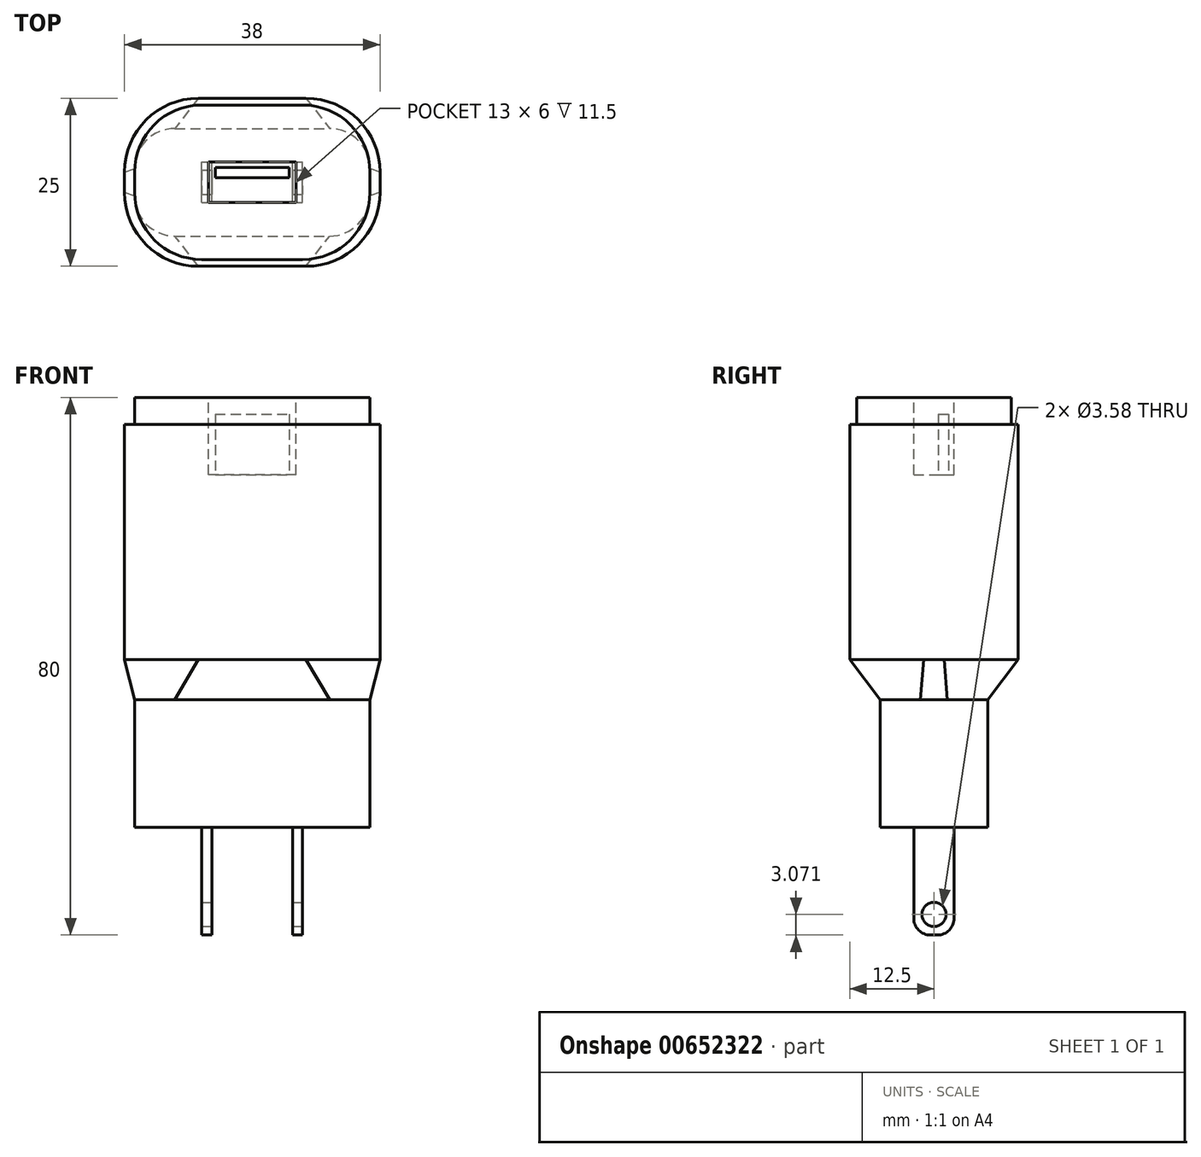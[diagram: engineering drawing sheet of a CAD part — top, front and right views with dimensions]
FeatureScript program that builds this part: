
annotation { "Feature Type Name" : "Feature", "Feature Type Description" : "" }
export const myFeature = defineFeature(function(context is Context, id is Id, definition is map)
    precondition{}
    {
        {
            var Q0;
            Q0=qCreatedBy(makeId("Top.planeOp"),FACE);
            var sketch = newSketch(context, id + "F0", { "sketchPlane" : qUnion([Q0])});
            skLineSegment(sketch, "E0.bottom", {"start": v(-19, -12.5) * mm, "end": v(19, -12.5) * mm});
            skLineSegment(sketch, "E0.top", {"start": v(-19, 12.5) * mm, "end": v(19, 12.5) * mm});
            skLineSegment(sketch, "E0.left", {"start": v(-19, -12.5) * mm, "end": v(-19, 12.5) * mm});
            skLineSegment(sketch, "E0.right", {"start": v(19, -12.5) * mm, "end": v(19, 12.5) * mm});
            skPoint(sketch, "E0.middle", {"position": v(0, 0) * mm});
            skSolve(sketch);
        }
        {
            var Q0;
            Q0=makeQuery(id+"F0.imprint","IMPRINT",FACE,{"disambiguationData":[TD([[makeQuery(id+"F0.imprint","IMPRINT",EDGE,{"derivedFrom":sQuery(id+"F0.wireOp",EDGE,"E0.bottom")}),1.0]])]});
            extrude(context, id + "F1", {"entities" : qUnion([Q0]), "depth" : 35 * mm, "offsetDistance" : 25.4 * mm});
        }
        {
            var Q0;
            Q0=makeQuery(id+"F1.opExtrude","SWEPT_EDGE",EDGE,{"disambiguationData":[OSD([sQuery(id+"F0.wireOp",EDGE,"E0.bottom"),sQuery(id+"F0.wireOp",EDGE,"E0.right")])]});
            var Q1;
            Q1=makeQuery(id+"F1.opExtrude","SWEPT_EDGE",EDGE,{"disambiguationData":[OSD([sQuery(id+"F0.wireOp",EDGE,"E0.bottom"),sQuery(id+"F0.wireOp",EDGE,"E0.left")])]});
            var Q2;
            Q2=makeQuery(id+"F1.opExtrude","SWEPT_EDGE",EDGE,{"disambiguationData":[OSD([sQuery(id+"F0.wireOp",EDGE,"E0.top"),sQuery(id+"F0.wireOp",EDGE,"E0.right")])]});
            var Q3;
            Q3=makeQuery(id+"F1.opExtrude","SWEPT_EDGE",EDGE,{"disambiguationData":[OSD([sQuery(id+"F0.wireOp",EDGE,"E0.top"),sQuery(id+"F0.wireOp",EDGE,"E0.left")])]});
            fillet(context, id + "F2", {"entities" : qUnion([Q0, Q1, Q2, Q3]), "radius" : 11 * mm, "tangentPropagation" : true, "allowEdgeOverflow" : false});
        }
        {
            var Q0;
            Q0=qCreatedBy(makeId("Top.planeOp"),FACE);
            var sketch = newSketch(context, id + "F3", { "sketchPlane" : qUnion([Q0])});
            skLineSegment(sketch, "E1.bottom", {"start": v(17.5, -11.5) * mm, "end": v(-17.5, -11.5) * mm});
            skLineSegment(sketch, "E1.top", {"start": v(17.5, 11.5) * mm, "end": v(-17.5, 11.5) * mm});
            skLineSegment(sketch, "E1.left", {"start": v(17.5, -11.5) * mm, "end": v(17.5, 11.5) * mm});
            skLineSegment(sketch, "E1.right", {"start": v(-17.5, -11.5) * mm, "end": v(-17.5, 11.5) * mm});
            skPoint(sketch, "E1.middle", {"position": v(0, 0) * mm});
            skSolve(sketch);
        }
        {
            var Q0;
            Q0 = qSketchRegion(id + "F3", true);
            extrude(context, id + "F4", {"entities" : qUnion([Q0]), "operationType" : NewBodyOperationType.ADD, "depth" : 39 * mm, "offsetDistance" : 25 * mm});
        }
        {
            var Q0;
            Q0=makeQuery(id+"F4.opExtrude","SWEPT_EDGE",EDGE,{"disambiguationData":[OSD([sQuery(id+"F3.wireOp",EDGE,"E1.bottom"),sQuery(id+"F3.wireOp",EDGE,"E1.right")])]});
            var Q1;
            Q1=makeQuery(id+"F4.opExtrude","SWEPT_EDGE",EDGE,{"disambiguationData":[OSD([sQuery(id+"F3.wireOp",EDGE,"E1.bottom"),sQuery(id+"F3.wireOp",EDGE,"E1.left")])]});
            var Q2;
            Q2=makeQuery(id+"F4.opExtrude","SWEPT_EDGE",EDGE,{"disambiguationData":[OSD([sQuery(id+"F3.wireOp",EDGE,"E1.top"),sQuery(id+"F3.wireOp",EDGE,"E1.left")])]});
            var Q3;
            Q3=makeQuery(id+"F4.opExtrude","SWEPT_EDGE",EDGE,{"disambiguationData":[OSD([sQuery(id+"F3.wireOp",EDGE,"E1.top"),sQuery(id+"F3.wireOp",EDGE,"E1.right")])]});
            fillet(context, id + "F5", {"entities" : qUnion([Q0, Q1, Q2, Q3]), "radius" : 10 * mm, "tangentPropagation" : true, "allowEdgeOverflow" : false});
        }
        {
            var Q0;
            Q0=makeQuery(id+"F4.opExtrude","CAP_FACE",FACE,{"disambiguationData":[OSD([sQuery(id+"F3.wireOp",EDGE,"E1.bottom"),sQuery(id+"F3.wireOp",EDGE,"E1.top"),sQuery(id+"F3.wireOp",EDGE,"E1.left"),sQuery(id+"F3.wireOp",EDGE,"E1.right")])],"isStart":false});
            var sketch = newSketch(context, id + "F6", { "sketchPlane" : qUnion([Q0])});
            skLineSegment(sketch, "E2.bottom", {"start": v(6.5, -3) * mm, "end": v(-6.5, -3) * mm});
            skLineSegment(sketch, "E2.top", {"start": v(6.5, 3) * mm, "end": v(-6.5, 3) * mm});
            skLineSegment(sketch, "E2.left", {"start": v(6.5, -3) * mm, "end": v(6.5, 3) * mm});
            skLineSegment(sketch, "E2.right", {"start": v(-6.5, -3) * mm, "end": v(-6.5, 3) * mm});
            skPoint(sketch, "E2.middle", {"position": v(0, 0) * mm});
            skSolve(sketch);
        }
        {
            var Q0;
            Q0=makeQuery(id+"F6.imprint","IMPRINT",FACE,{"disambiguationData":[TD([[makeQuery(id+"F6.imprint","IMPRINT",EDGE,{"derivedFrom":sQuery(id+"F6.wireOp",EDGE,"E2.bottom")}),-1.0]])]});
            extrude(context, id + "F7", {"entities" : qUnion([Q0]), "operationType" : NewBodyOperationType.REMOVE, "oppositeDirection" : true, "depth" : 11.5 * mm, "offsetDistance" : 25 * mm});
        }
        {
            var Q0;
            Q0=makeQuery(id+"F7.boolean.opBoolean","COPY",FACE,{"derivedFrom":makeQuery(id+"F7.opExtrude","CAP_FACE",FACE,{"disambiguationData":[OSD([sQuery(id+"F6.wireOp",EDGE,"E2.bottom"),sQuery(id+"F6.wireOp",EDGE,"E2.top"),sQuery(id+"F6.wireOp",EDGE,"E2.left"),sQuery(id+"F6.wireOp",EDGE,"E2.right")])],"isStart":false})});
            var sketch = newSketch(context, id + "F8", { "sketchPlane" : qUnion([Q0])});
            skLineSegment(sketch, "E3.bottom", {"start": v(-5.5, 0.67) * mm, "end": v(5.5, 0.67) * mm});
            skLineSegment(sketch, "E3.top", {"start": v(-5.5, 2.17) * mm, "end": v(5.5, 2.17) * mm});
            skLineSegment(sketch, "E3.left", {"start": v(-5.5, 0.67) * mm, "end": v(-5.5, 2.17) * mm});
            skLineSegment(sketch, "E3.right", {"start": v(5.5, 0.67) * mm, "end": v(5.5, 2.17) * mm});
            skSolve(sketch);
        }
        {
            var Q0;
            Q0=makeQuery(id+"F8.imprint","IMPRINT",FACE,{"disambiguationData":[TD([[makeQuery(id+"F8.imprint","IMPRINT",EDGE,{"derivedFrom":sQuery(id+"F8.wireOp",EDGE,"E3.bottom")}),1.0]])]});
            extrude(context, id + "F9", {"entities" : qUnion([Q0]), "depth" : 9 * mm, "offsetDistance" : 25 * mm});
        }
        {
            var Q0;
            Q0=qCreatedBy(makeId("Top.planeOp"),FACE);
            var sketch = newSketch(context, id + "F10", { "sketchPlane" : qUnion([Q0])});
            skLineSegment(sketch, "E4.bottom", {"start": v(17.5, -8) * mm, "end": v(-17.5, -8) * mm});
            skLineSegment(sketch, "E4.top", {"start": v(17.5, 8) * mm, "end": v(-17.5, 8) * mm});
            skLineSegment(sketch, "E4.left", {"start": v(17.5, -8) * mm, "end": v(17.5, 8) * mm});
            skLineSegment(sketch, "E4.right", {"start": v(-17.5, -8) * mm, "end": v(-17.5, 8) * mm});
            skPoint(sketch, "E4.middle", {"position": v(0, 0) * mm});
            skSolve(sketch);
        }
        {
            var Q0;
            Q0=makeQuery(id+"F10.imprint","IMPRINT",FACE,{"disambiguationData":[TD([[makeQuery(id+"F10.imprint","IMPRINT",EDGE,{"derivedFrom":sQuery(id+"F10.wireOp",EDGE,"E4.bottom")}),-1.0]])]});
            var Q1;
            Q1 = qSketchRegion(id + "F13", true);
            extrude(context, id + "F11", {"entities" : qUnion([Q0, Q1]), "operationType" : NewBodyOperationType.ADD, "oppositeDirection" : true, "depth" : 24 * mm, "offsetDistance" : 25 * mm});
        }
        {
            var Q0;
            Q0=makeQuery(id+"F11.opExtrude","SWEPT_EDGE",EDGE,{"disambiguationData":[OSD([sQuery(id+"F10.wireOp",EDGE,"E4.top"),sQuery(id+"F10.wireOp",EDGE,"E4.left")])]});
            var Q1;
            Q1=makeQuery(id+"F11.opExtrude","SWEPT_EDGE",EDGE,{"disambiguationData":[OSD([sQuery(id+"F10.wireOp",EDGE,"E4.top"),sQuery(id+"F10.wireOp",EDGE,"E4.right")])]});
            var Q2;
            Q2=makeQuery(id+"F11.opExtrude","SWEPT_EDGE",EDGE,{"disambiguationData":[OSD([sQuery(id+"F10.wireOp",EDGE,"E4.bottom"),sQuery(id+"F10.wireOp",EDGE,"E4.left")])]});
            var Q3;
            Q3=makeQuery(id+"F11.opExtrude","SWEPT_EDGE",EDGE,{"disambiguationData":[OSD([sQuery(id+"F10.wireOp",EDGE,"E4.bottom"),sQuery(id+"F10.wireOp",EDGE,"E4.right")])]});
            fillet(context, id + "F12", {"entities" : qUnion([Q0, Q1, Q2, Q3]), "radius" : 6 * mm, "tangentPropagation" : true, "allowEdgeOverflow" : false});
        }
        {
            var Q0;
            Q0=qCreatedBy(makeId("Top.planeOp"),FACE);
            var sketch = newSketch(context, id + "F13", { "sketchPlane" : qUnion([Q0])});
            skLineSegment(sketch, "E5.bottom", {"start": v(-40.38, 25.75) * mm, "end": v(40.38, 25.75) * mm});
            skLineSegment(sketch, "E5.top", {"start": v(-40.38, -25.75) * mm, "end": v(40.38, -25.75) * mm});
            skLineSegment(sketch, "E5.left", {"start": v(-40.38, 25.75) * mm, "end": v(-40.38, -25.75) * mm});
            skLineSegment(sketch, "E5.right", {"start": v(40.38, 25.75) * mm, "end": v(40.38, -25.75) * mm});
            skPoint(sketch, "E5.middle", {"position": v(0, 0) * mm});
            skSolve(sketch);
        }
        {
            var Q0;
            Q0=makeQuery(id+"F13.imprint","IMPRINT",FACE,{"disambiguationData":[TD([[makeQuery(id+"F13.imprint","IMPRINT",EDGE,{"derivedFrom":sQuery(id+"F13.wireOp",EDGE,"E5.bottom")}),-1.0]])]});
            extrude(context, id + "F14", {"entities" : qUnion([Q0]), "operationType" : NewBodyOperationType.REMOVE, "oppositeDirection" : true, "depth" : 6 * mm, "offsetDistance" : 25 * mm});
        }
        {
            var Q0;
            {var subQ0=sQuery(id+"F0.wireOp",EDGE,"E0.right");var subQ1=sQuery(id+"F0.wireOp",EDGE,"E0.top");var subQ8=sQuery(id+"F0.wireOp",EDGE,"E0.left");var subQ10=sQuery(id+"F0.wireOp",EDGE,"E0.bottom");var subQ11=makeQuery(id+"F4.boolean.opBoolean","MERGE",FACE,{"derivedFrom":[makeQuery(id+"F1.opExtrude","CAP_FACE",FACE,{"disambiguationData":[OSD([subQ10,subQ1,subQ8,subQ0])],"isStart":true}),makeQuery(id+"F4.opExtrude","CAP_FACE",FACE,{"disambiguationData":[OSD([sQuery(id+"F3.wireOp",EDGE,"E1.bottom"),sQuery(id+"F3.wireOp",EDGE,"E1.top"),sQuery(id+"F3.wireOp",EDGE,"E1.left"),sQuery(id+"F3.wireOp",EDGE,"E1.right")])],"isStart":true})]});Q0=makeQuery(id+"F14.boolean.opBoolean","MERGE",FACE,{"derivedFrom":[makeQuery(id+"F12.opFillet","MERGE",FACE,{"derivedFrom":[makeQuery(id+"F11.boolean.opBoolean","SPLIT",FACE,{"disambiguationData":[TD([makeQuery(id+"F1.opExtrude","SWEPT_FACE",FACE,{"disambiguationData":[OSD([subQ8])]})])],"derivedFrom":subQ11}),makeQuery(id+"F11.boolean.opBoolean","SPLIT",FACE,{"disambiguationData":[TD([makeQuery(id+"F1.opExtrude","SWEPT_FACE",FACE,{"disambiguationData":[OSD([subQ0])]})])],"derivedFrom":subQ11}),makeQuery(id+"F11.boolean.opBoolean","SPLIT",FACE,{"disambiguationData":[TD([makeQuery(id+"F1.opExtrude","SWEPT_FACE",FACE,{"disambiguationData":[OSD([subQ10])]})])],"derivedFrom":subQ11}),makeQuery(id+"F11.boolean.opBoolean","SPLIT",FACE,{"disambiguationData":[TD([makeQuery(id+"F1.opExtrude","SWEPT_FACE",FACE,{"disambiguationData":[OSD([subQ1])]})])],"derivedFrom":subQ11})]}),makeQuery(id+"F14.opExtrude","CAP_FACE",FACE,{"disambiguationData":[OSD([sQuery(id+"F13.wireOp",EDGE,"E5.bottom"),sQuery(id+"F13.wireOp",EDGE,"E5.top"),sQuery(id+"F13.wireOp",EDGE,"E5.left"),sQuery(id+"F13.wireOp",EDGE,"E5.right")])],"isStart":true})]});}
            var Q1;
            Q1=makeQuery(id+"F14.boolean.opBoolean","COPY",FACE,{"derivedFrom":makeQuery(id+"F14.opExtrude","CAP_FACE",FACE,{"disambiguationData":[OSD([sQuery(id+"F13.wireOp",EDGE,"E5.bottom"),sQuery(id+"F13.wireOp",EDGE,"E5.top"),sQuery(id+"F13.wireOp",EDGE,"E5.left"),sQuery(id+"F13.wireOp",EDGE,"E5.right")])],"isStart":false})});
            loft(context, id + "F15", {"sheetProfilesArray" : [{ "sheetProfileEntities" : qUnion([Q0]) }, { "sheetProfileEntities" : qUnion([Q1]) }]});
        }
        {
            var Q0;
            Q0=makeQuery(id+"F11.opExtrude","CAP_FACE",FACE,{"disambiguationData":[OSD([sQuery(id+"F10.wireOp",EDGE,"E4.bottom"),sQuery(id+"F10.wireOp",EDGE,"E4.top"),sQuery(id+"F10.wireOp",EDGE,"E4.left"),sQuery(id+"F10.wireOp",EDGE,"E4.right")])],"isStart":false});
            extrude(context, id + "F16", {"entities" : qUnion([Q0]), "operationType" : NewBodyOperationType.ADD, "depth" : 1 * mm, "offsetDistance" : 25 * mm});
        }
        {
            var Q0;
            Q0=makeQuery(id+"F16.opExtrude","CAP_FACE",FACE,{"disambiguationData":[OSD([sQuery(id+"F10.wireOp",EDGE,"E4.bottom"),sQuery(id+"F10.wireOp",EDGE,"E4.top"),sQuery(id+"F10.wireOp",EDGE,"E4.left"),sQuery(id+"F10.wireOp",EDGE,"E4.right")])],"isStart":false});
            var sketch = newSketch(context, id + "F17", { "sketchPlane" : qUnion([Q0])});
            skLineSegment(sketch, "E6.bottom", {"start": v(-7.5, 3) * mm, "end": v(7.5, 3) * mm});
            skLineSegment(sketch, "E6.top", {"start": v(-7.5, -3) * mm, "end": v(7.5, -3) * mm});
            skLineSegment(sketch, "E6.left", {"start": v(-7.5, 3) * mm, "end": v(-7.5, -3) * mm});
            skLineSegment(sketch, "E6.right", {"start": v(7.5, 3) * mm, "end": v(7.5, -3) * mm});
            skPoint(sketch, "E6.middle", {"position": v(0, 0) * mm});
            skSolve(sketch);
        }
        {
            var Q0;
            Q0=makeQuery(id+"F17.imprint","IMPRINT",FACE,{"disambiguationData":[TD([[makeQuery(id+"F17.imprint","IMPRINT",EDGE,{"derivedFrom":sQuery(id+"F17.wireOp",EDGE,"E6.bottom")}),-1.0]])]});
            extrude(context, id + "F18", {"entities" : qUnion([Q0]), "operationType" : NewBodyOperationType.ADD, "depth" : 16 * mm, "offsetDistance" : 25 * mm});
        }
        {
            var Q0;
            Q0=makeQuery(id+"F18.opExtrude","CAP_EDGE",EDGE,{"disambiguationData":[OSD([sQuery(id+"F17.wireOp",EDGE,"E6.bottom")])],"isStart":false});
            var Q1;
            Q1=makeQuery(id+"F18.opExtrude","CAP_EDGE",EDGE,{"disambiguationData":[OSD([sQuery(id+"F17.wireOp",EDGE,"E6.top")])],"isStart":false});
            fillet(context, id + "F19", {"entities" : qUnion([Q0, Q1]), "radius" : 2.5 * mm, "tangentPropagation" : true, "allowEdgeOverflow" : false});
        }
        {
            var Q0;
            Q0=makeQuery(id+"F16.opExtrude","CAP_FACE",FACE,{"disambiguationData":[OSD([sQuery(id+"F10.wireOp",EDGE,"E4.bottom"),sQuery(id+"F10.wireOp",EDGE,"E4.top"),sQuery(id+"F10.wireOp",EDGE,"E4.left"),sQuery(id+"F10.wireOp",EDGE,"E4.right")])],"isStart":false});
            var sketch = newSketch(context, id + "F20", { "sketchPlane" : qUnion([Q0])});
            skLineSegment(sketch, "E7.bottom", {"start": v(-6, 3) * mm, "end": v(6, 3) * mm});
            skLineSegment(sketch, "E7.top", {"start": v(-6, -3) * mm, "end": v(6, -3) * mm});
            skLineSegment(sketch, "E7.left", {"start": v(-6, 3) * mm, "end": v(-6, -3) * mm});
            skLineSegment(sketch, "E7.right", {"start": v(6, 3) * mm, "end": v(6, -3) * mm});
            skPoint(sketch, "E7.middle", {"position": v(0, 0) * mm});
            skSolve(sketch);
        }
        {
            var Q0;
            Q0 = qSketchRegion(id + "F20", true);
            extrude(context, id + "F21", {"entities" : qUnion([Q0]), "operationType" : NewBodyOperationType.REMOVE, "endBound" : BoundingType.THROUGH_ALL, "depth" : 25 * mm, "offsetDistance" : 25 * mm});
        }
        {
            var Q0;
            Q0=makeQuery(id+"F18.opExtrude","SWEPT_FACE",FACE,{"disambiguationData":[OSD([sQuery(id+"F17.wireOp",EDGE,"E6.right")])]});
            var sketch = newSketch(context, id + "F22", { "sketchPlane" : qUnion([Q0])});
            skCircle(sketch, "E8", {"center": v(0, -37.93) * mm, "radius": 1.8 * mm});
            skSolve(sketch);
        }
        {
            var Q0;
            Q0=makeQuery(id+"F22.imprint","IMPRINT",FACE,{"disambiguationData":[TD([[makeQuery(id+"F22.imprint","IMPRINT",EDGE,{"derivedFrom":sQuery(id+"F22.wireOp",EDGE,"E8")}),1.0]])]});
            var Q1;
            Q1=sQuery(id+"F22.wireOp",EDGE,"E8");
            extrude(context, id + "F23", {"entities" : qUnion([Q0]), "operationType" : NewBodyOperationType.REMOVE, "surfaceEntities" : qUnion([Q1]), "endBound" : BoundingType.THROUGH_ALL, "oppositeDirection" : true, "depth" : 25 * mm, "offsetDistance" : 25 * mm});
        }
    });
